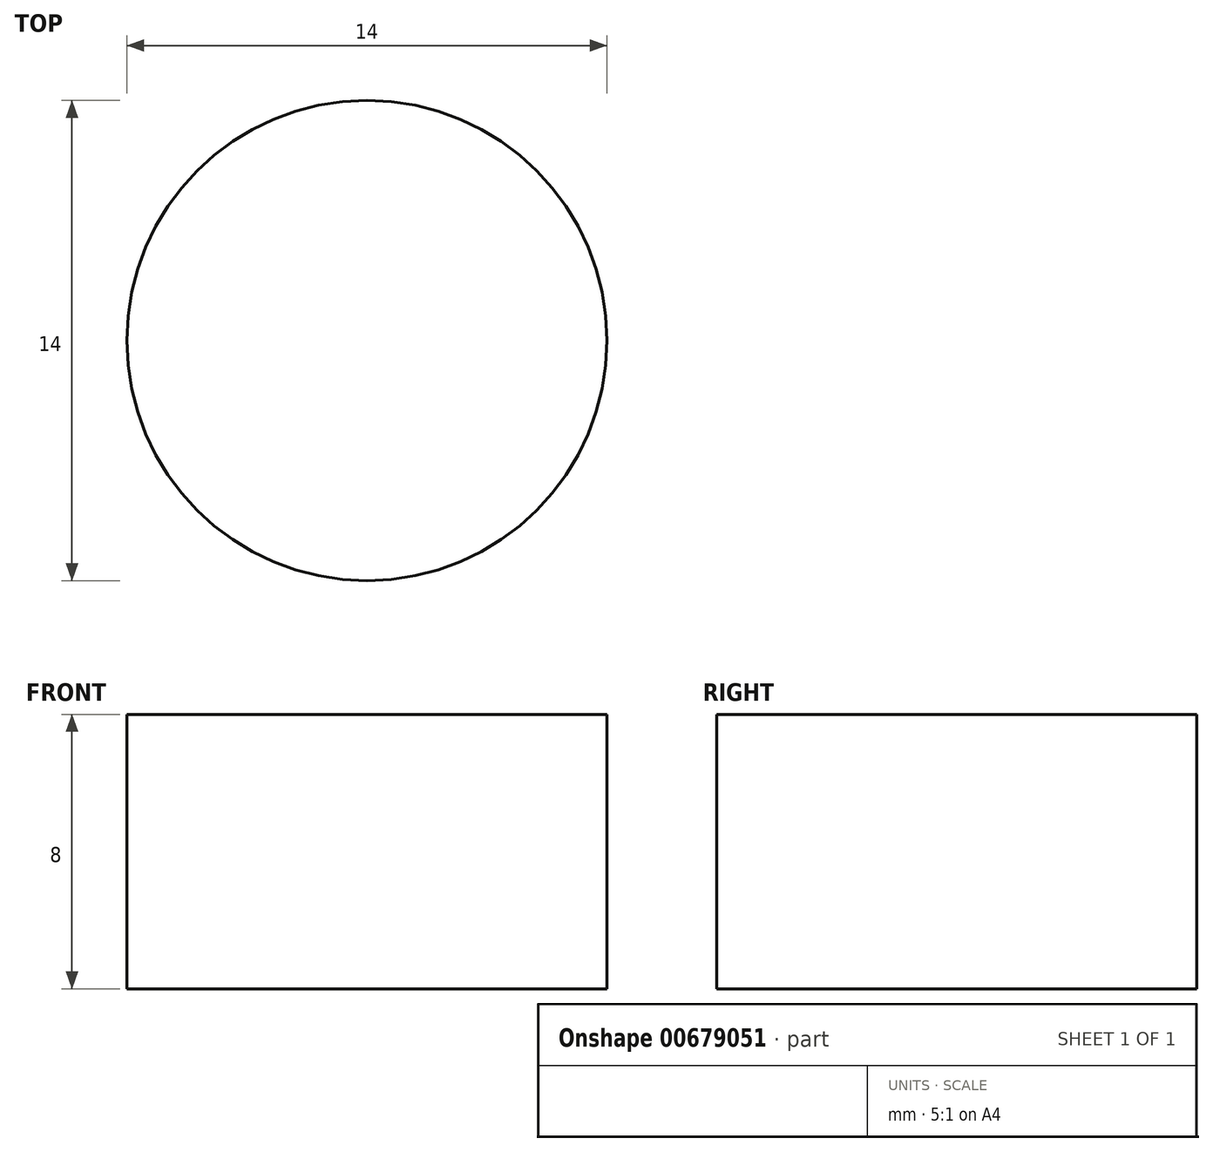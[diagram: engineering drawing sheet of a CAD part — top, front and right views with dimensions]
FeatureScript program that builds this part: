
annotation { "Feature Type Name" : "Feature", "Feature Type Description" : "" }
export const myFeature = defineFeature(function(context is Context, id is Id, definition is map)
    precondition{}
    {
        {
            var Q0;
            Q0=qCreatedBy(makeId("Top.planeOp"),FACE);
            var sketch = newSketch(context, id + "F0", { "sketchPlane" : qUnion([Q0])});
            skCircle(sketch, "E0", {"center": v(0, 0) * mm, "radius": 7 * mm});
            skSolve(sketch);
        }
        {
            var Q0;
            Q0=qSketchRegion(id+"F0",true);
            extrude(context, id + "F1", {"entities" : qUnion([Q0]), "depth" : 8 * mm, "offsetDistance" : 25 * mm});
        }
    });
